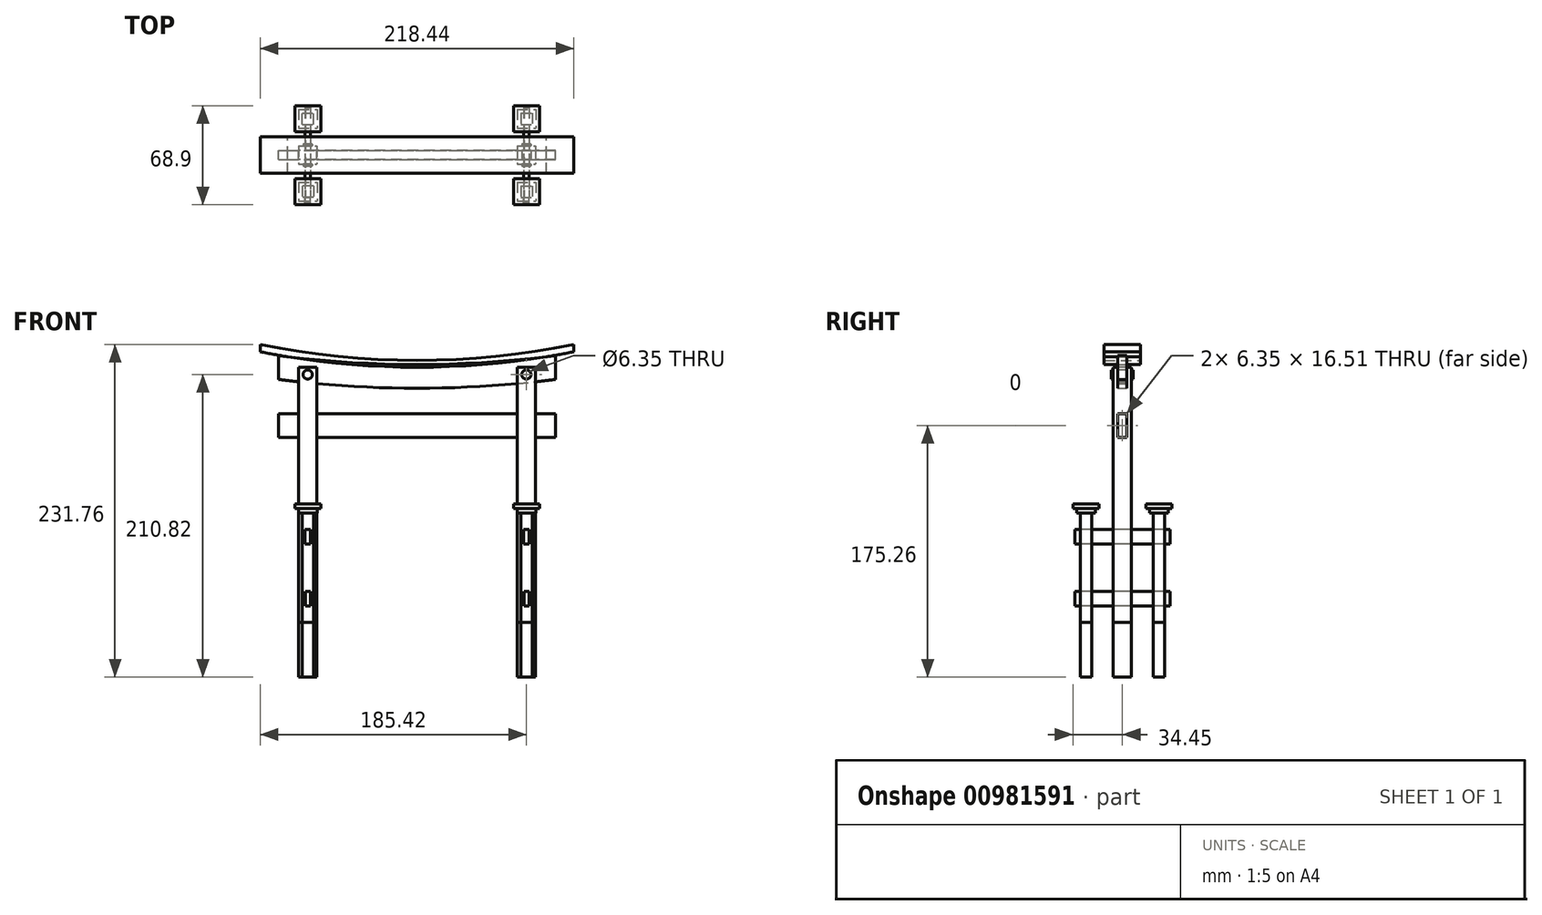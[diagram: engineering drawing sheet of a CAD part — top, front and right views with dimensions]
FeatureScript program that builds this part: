
annotation { "Feature Type Name" : "Feature", "Feature Type Description" : "" }
export const myFeature = defineFeature(function(context is Context, id is Id, definition is map)
    precondition{}
    {
        {
            var Q0;
            Q0=qCreatedBy(makeId("Top.planeOp"),FACE);
            var sketch = newSketch(context, id + "F0", { "sketchPlane" : qUnion([Q0])});
            skLineSegment(sketch, "E0.bottom", {"start": v(-82.55, 6.35) * mm, "end": v(-69.85, 6.35) * mm});
            skLineSegment(sketch, "E0.top", {"start": v(-82.55, -6.35) * mm, "end": v(-69.85, -6.35) * mm});
            skLineSegment(sketch, "E0.left", {"start": v(-82.55, 6.35) * mm, "end": v(-82.55, -6.35) * mm});
            skLineSegment(sketch, "E0.right", {"start": v(-69.85, 6.35) * mm, "end": v(-69.85, -6.35) * mm});
            skPoint(sketch, "E0.middle", {"position": v(-76.2, 0) * mm});
            skLineSegment(sketch, "E1.bottom", {"start": v(69.85, 6.35) * mm, "end": v(82.55, 6.35) * mm});
            skLineSegment(sketch, "E1.top", {"start": v(69.85, -6.35) * mm, "end": v(82.55, -6.35) * mm});
            skLineSegment(sketch, "E1.left", {"start": v(69.85, 6.35) * mm, "end": v(69.85, -6.35) * mm});
            skLineSegment(sketch, "E1.right", {"start": v(82.55, 6.35) * mm, "end": v(82.55, -6.35) * mm});
            skPoint(sketch, "E1.middle", {"position": v(76.2, 0) * mm});
            skLineSegment(sketch, "E2", {"start": v(-69.85, 0) * mm, "end": v(0, 0) * mm, "construction": true});
            skLineSegment(sketch, "E3", {"start": v(0, 0) * mm, "end": v(69.85, 0) * mm, "construction": true});
            skLineSegment(sketch, "E4.bottom", {"start": v(-80.17, 21.43) * mm, "end": v(-72.23, 21.43) * mm});
            skLineSegment(sketch, "E4.top", {"start": v(-80.17, 29.37) * mm, "end": v(-72.23, 29.37) * mm});
            skLineSegment(sketch, "E4.left", {"start": v(-80.17, 21.43) * mm, "end": v(-80.17, 29.37) * mm});
            skLineSegment(sketch, "E4.right", {"start": v(-72.23, 21.43) * mm, "end": v(-72.23, 29.37) * mm});
            skPoint(sketch, "E4.middle", {"position": v(-76.2, 25.4) * mm});
            skLineSegment(sketch, "E5.bottom", {"start": v(72.23, 29.37) * mm, "end": v(80.17, 29.37) * mm});
            skLineSegment(sketch, "E5.top", {"start": v(72.23, 21.43) * mm, "end": v(80.17, 21.43) * mm});
            skLineSegment(sketch, "E5.left", {"start": v(72.23, 29.37) * mm, "end": v(72.23, 21.43) * mm});
            skLineSegment(sketch, "E5.right", {"start": v(80.17, 29.37) * mm, "end": v(80.17, 21.43) * mm});
            skPoint(sketch, "E5.middle", {"position": v(76.2, 25.4) * mm});
            skLineSegment(sketch, "E6.bottom", {"start": v(72.23, -21.43) * mm, "end": v(80.17, -21.43) * mm});
            skLineSegment(sketch, "E6.top", {"start": v(72.23, -29.37) * mm, "end": v(80.17, -29.37) * mm});
            skLineSegment(sketch, "E6.left", {"start": v(72.23, -21.43) * mm, "end": v(72.23, -29.37) * mm});
            skLineSegment(sketch, "E6.right", {"start": v(80.17, -21.43) * mm, "end": v(80.17, -29.37) * mm});
            skPoint(sketch, "E6.middle", {"position": v(76.2, -25.4) * mm});
            skLineSegment(sketch, "E7.bottom", {"start": v(-72.23, -21.43) * mm, "end": v(-80.17, -21.43) * mm});
            skLineSegment(sketch, "E7.top", {"start": v(-72.23, -29.37) * mm, "end": v(-80.17, -29.37) * mm});
            skLineSegment(sketch, "E7.left", {"start": v(-72.23, -21.43) * mm, "end": v(-72.23, -29.37) * mm});
            skLineSegment(sketch, "E7.right", {"start": v(-80.17, -21.43) * mm, "end": v(-80.17, -29.37) * mm});
            skPoint(sketch, "E7.middle", {"position": v(-76.2, -25.4) * mm});
            skLineSegment(sketch, "E8", {"start": v(-76.2, 0) * mm, "end": v(-76.2, 25.4) * mm, "construction": true});
            skLineSegment(sketch, "E9", {"start": v(-76.2, 0) * mm, "end": v(-76.2, -25.4) * mm, "construction": true});
            skLineSegment(sketch, "E10", {"start": v(76.2, 0) * mm, "end": v(76.2, -25.4) * mm, "construction": true});
            skLineSegment(sketch, "E11", {"start": v(76.2, 25.4) * mm, "end": v(76.2, 0) * mm, "construction": true});
            skSolve(sketch);
        }
        {
            var Q0;
            Q0=makeQuery(id+"F0.imprint","IMPRINT",FACE,{"disambiguationData":[TD([[makeQuery(id+"F0.imprint","IMPRINT",EDGE,{"derivedFrom":sQuery(id+"F0.wireOp",EDGE,"E0.bottom")}),-1.0]])]});
            var Q1;
            Q1=makeQuery(id+"F0.imprint","IMPRINT",FACE,{"disambiguationData":[TD([[makeQuery(id+"F0.imprint","IMPRINT",EDGE,{"derivedFrom":sQuery(id+"F0.wireOp",EDGE,"E1.bottom")}),-1.0]])]});
            extrude(context, id + "F1", {"entities" : qUnion([Q0, Q1]), "depth" : 177.8 * mm, "offsetDistance" : 25.4 * mm});
        }
        {
            var Q0;
            Q0=makeQuery(id+"F0.imprint","IMPRINT",FACE,{"disambiguationData":[TD([[makeQuery(id+"F0.imprint","IMPRINT",EDGE,{"derivedFrom":sQuery(id+"F0.wireOp",EDGE,"E7.bottom")}),1.0]])]});
            var Q1;
            Q1=makeQuery(id+"F0.imprint","IMPRINT",FACE,{"disambiguationData":[TD([[makeQuery(id+"F0.imprint","IMPRINT",EDGE,{"derivedFrom":sQuery(id+"F0.wireOp",EDGE,"E4.bottom")}),1.0]])]});
            var Q2;
            Q2=makeQuery(id+"F0.imprint","IMPRINT",FACE,{"disambiguationData":[TD([[makeQuery(id+"F0.imprint","IMPRINT",EDGE,{"derivedFrom":sQuery(id+"F0.wireOp",EDGE,"E6.bottom")}),-1.0]])]});
            var Q3;
            Q3=makeQuery(id+"F0.imprint","IMPRINT",FACE,{"disambiguationData":[TD([[makeQuery(id+"F0.imprint","IMPRINT",EDGE,{"derivedFrom":sQuery(id+"F0.wireOp",EDGE,"E5.bottom")}),-1.0]])]});
            extrude(context, id + "F2", {"entities" : qUnion([Q0, Q1, Q2, Q3]), "depth" : 76.2 * mm, "offsetDistance" : 25.4 * mm});
        }
        {
            var Q0;
            Q0=makeQuery(id+"F2.opExtrude","CAP_FACE",FACE,{"disambiguationData":[OSD([sQuery(id+"F0.wireOp",EDGE,"E4.bottom"),sQuery(id+"F0.wireOp",EDGE,"E4.top"),sQuery(id+"F0.wireOp",EDGE,"E4.left"),sQuery(id+"F0.wireOp",EDGE,"E4.right")])],"isStart":false});
            var sketch = newSketch(context, id + "F3", { "sketchPlane" : qUnion([Q0])});
            skLineSegment(sketch, "E12.0.0", {"start": v(-72.23, 29.37) * mm, "end": v(-80.17, 29.37) * mm});
            skLineSegment(sketch, "E12.0.1", {"start": v(-80.17, 29.37) * mm, "end": v(-80.17, 21.43) * mm});
            skLineSegment(sketch, "E12.0.2", {"start": v(-80.17, 21.43) * mm, "end": v(-72.23, 21.43) * mm});
            skLineSegment(sketch, "E12.0.3", {"start": v(-72.23, 21.43) * mm, "end": v(-72.23, 29.37) * mm});
            skLineSegment(sketch, "E13.0.0", {"start": v(-80.17, -29.37) * mm, "end": v(-72.23, -29.37) * mm});
            skLineSegment(sketch, "E13.0.1", {"start": v(-72.23, -29.37) * mm, "end": v(-72.23, -21.43) * mm});
            skLineSegment(sketch, "E13.0.2", {"start": v(-72.23, -21.43) * mm, "end": v(-80.17, -21.43) * mm});
            skLineSegment(sketch, "E13.0.3", {"start": v(-80.17, -21.43) * mm, "end": v(-80.17, -29.37) * mm});
            skLineSegment(sketch, "E14.0.0", {"start": v(72.23, -21.43) * mm, "end": v(72.23, -29.37) * mm});
            skLineSegment(sketch, "E14.0.1", {"start": v(72.23, -29.37) * mm, "end": v(80.17, -29.37) * mm});
            skLineSegment(sketch, "E14.0.2", {"start": v(80.17, -29.37) * mm, "end": v(80.17, -21.43) * mm});
            skLineSegment(sketch, "E14.0.3", {"start": v(80.17, -21.43) * mm, "end": v(72.23, -21.43) * mm});
            skLineSegment(sketch, "E15.0.0", {"start": v(72.23, 29.37) * mm, "end": v(72.23, 21.43) * mm});
            skLineSegment(sketch, "E15.0.1", {"start": v(72.23, 21.43) * mm, "end": v(80.17, 21.43) * mm});
            skLineSegment(sketch, "E15.0.2", {"start": v(80.17, 21.43) * mm, "end": v(80.17, 29.37) * mm});
            skLineSegment(sketch, "E15.0.3", {"start": v(80.17, 29.37) * mm, "end": v(72.23, 29.37) * mm});
            skPoint(sketch, "E16.0", {"position": v(-76.2, 25.4) * mm});
            skPoint(sketch, "E17.0", {"position": v(-76.2, -25.4) * mm});
            skPoint(sketch, "E18.0", {"position": v(76.2, -25.4) * mm});
            skPoint(sketch, "E19.0", {"position": v(76.2, 25.4) * mm});
            skLineSegment(sketch, "E20.bottom", {"start": v(-82.7, 31.9) * mm, "end": v(-69.7, 31.9) * mm});
            skLineSegment(sketch, "E20.top", {"start": v(-82.7, 18.9) * mm, "end": v(-69.7, 18.9) * mm});
            skLineSegment(sketch, "E20.left", {"start": v(-82.7, 31.9) * mm, "end": v(-82.7, 18.9) * mm});
            skLineSegment(sketch, "E20.right", {"start": v(-69.7, 31.9) * mm, "end": v(-69.7, 18.9) * mm});
            skLineSegment(sketch, "E21.bottom", {"start": v(-82.7, -18.9) * mm, "end": v(-69.7, -18.9) * mm});
            skLineSegment(sketch, "E21.top", {"start": v(-82.7, -31.9) * mm, "end": v(-69.7, -31.9) * mm});
            skLineSegment(sketch, "E21.left", {"start": v(-82.7, -18.9) * mm, "end": v(-82.7, -31.9) * mm});
            skLineSegment(sketch, "E21.right", {"start": v(-69.7, -18.9) * mm, "end": v(-69.7, -31.9) * mm});
            skLineSegment(sketch, "E22.bottom", {"start": v(69.7, 31.9) * mm, "end": v(82.7, 31.9) * mm});
            skLineSegment(sketch, "E22.top", {"start": v(69.7, 18.9) * mm, "end": v(82.7, 18.9) * mm});
            skLineSegment(sketch, "E22.left", {"start": v(69.7, 31.9) * mm, "end": v(69.7, 18.9) * mm});
            skLineSegment(sketch, "E22.right", {"start": v(82.7, 31.9) * mm, "end": v(82.7, 18.9) * mm});
            skLineSegment(sketch, "E23.bottom", {"start": v(69.7, -18.9) * mm, "end": v(82.7, -18.9) * mm});
            skLineSegment(sketch, "E23.top", {"start": v(69.7, -31.9) * mm, "end": v(82.7, -31.9) * mm});
            skLineSegment(sketch, "E23.left", {"start": v(69.7, -18.9) * mm, "end": v(69.7, -31.9) * mm});
            skLineSegment(sketch, "E23.right", {"start": v(82.7, -18.9) * mm, "end": v(82.7, -31.9) * mm});
            skSolve(sketch);
        }
        {
            var Q0;
            Q0=makeQuery(id+"F3.imprint","IMPRINT",FACE,{"disambiguationData":[TD([[makeQuery(id+"F3.imprint","IMPRINT",EDGE,{"derivedFrom":sQuery(id+"F3.wireOp",EDGE,"E12.0.0")}),1.0]])]});
            var Q1;
            Q1=makeQuery(id+"F3.imprint","IMPRINT",FACE,{"disambiguationData":[TD([[makeQuery(id+"F3.imprint","IMPRINT",EDGE,{"derivedFrom":sQuery(id+"F3.wireOp",EDGE,"E12.0.0")}),-1.0]])]});
            var Q2;
            Q2=makeQuery(id+"F3.imprint","IMPRINT",FACE,{"disambiguationData":[TD([[makeQuery(id+"F3.imprint","IMPRINT",EDGE,{"derivedFrom":sQuery(id+"F3.wireOp",EDGE,"E15.0.0")}),1.0]])]});
            var Q3;
            Q3=makeQuery(id+"F3.imprint","IMPRINT",FACE,{"disambiguationData":[TD([[makeQuery(id+"F3.imprint","IMPRINT",EDGE,{"derivedFrom":sQuery(id+"F3.wireOp",EDGE,"E15.0.0")}),-1.0]])]});
            var Q4;
            Q4=makeQuery(id+"F3.imprint","IMPRINT",FACE,{"disambiguationData":[TD([[makeQuery(id+"F3.imprint","IMPRINT",EDGE,{"derivedFrom":sQuery(id+"F3.wireOp",EDGE,"E14.0.0")}),1.0]])]});
            var Q5;
            Q5=makeQuery(id+"F3.imprint","IMPRINT",FACE,{"disambiguationData":[TD([[makeQuery(id+"F3.imprint","IMPRINT",EDGE,{"derivedFrom":sQuery(id+"F3.wireOp",EDGE,"E14.0.0")}),-1.0]])]});
            var Q6;
            Q6=makeQuery(id+"F3.imprint","IMPRINT",FACE,{"disambiguationData":[TD([[makeQuery(id+"F3.imprint","IMPRINT",EDGE,{"derivedFrom":sQuery(id+"F3.wireOp",EDGE,"E13.0.0")}),-1.0]])]});
            var Q7;
            Q7=makeQuery(id+"F3.imprint","IMPRINT",FACE,{"disambiguationData":[TD([[makeQuery(id+"F3.imprint","IMPRINT",EDGE,{"derivedFrom":sQuery(id+"F3.wireOp",EDGE,"E13.0.0")}),1.0]])]});
            extrude(context, id + "F4", {"entities" : qUnion([Q0, Q1, Q2, Q3, Q4, Q5, Q6, Q7]), "depth" : 3.17 * mm, "offsetDistance" : 25.4 * mm});
        }
        {
            var Q0;
            Q0=makeQuery(id+"F4.opExtrude","CAP_FACE",FACE,{"disambiguationData":[OSD([sQuery(id+"F3.wireOp",EDGE,"E20.bottom"),sQuery(id+"F3.wireOp",EDGE,"E20.top"),sQuery(id+"F3.wireOp",EDGE,"E20.left"),sQuery(id+"F3.wireOp",EDGE,"E20.right")])],"isStart":false});
            var sketch = newSketch(context, id + "F5", { "sketchPlane" : qUnion([Q0])});
            skLineSegment(sketch, "E24.0.0", {"start": v(-82.7, 31.9) * mm, "end": v(-82.7, 18.9) * mm});
            skLineSegment(sketch, "E24.0.1", {"start": v(-82.7, 18.9) * mm, "end": v(-69.7, 18.9) * mm});
            skLineSegment(sketch, "E24.0.2", {"start": v(-69.7, 18.9) * mm, "end": v(-69.7, 31.9) * mm});
            skLineSegment(sketch, "E24.0.3", {"start": v(-69.7, 31.9) * mm, "end": v(-82.7, 31.9) * mm});
            skLineSegment(sketch, "E25.0.0", {"start": v(-82.7, -18.9) * mm, "end": v(-82.7, -31.9) * mm});
            skLineSegment(sketch, "E25.0.1", {"start": v(-82.7, -31.9) * mm, "end": v(-69.7, -31.9) * mm});
            skLineSegment(sketch, "E25.0.2", {"start": v(-69.7, -31.9) * mm, "end": v(-69.7, -18.9) * mm});
            skLineSegment(sketch, "E25.0.3", {"start": v(-69.7, -18.9) * mm, "end": v(-82.7, -18.9) * mm});
            skLineSegment(sketch, "E26.0.0", {"start": v(69.7, 31.9) * mm, "end": v(69.7, 18.9) * mm});
            skLineSegment(sketch, "E26.0.1", {"start": v(69.7, 18.9) * mm, "end": v(82.7, 18.9) * mm});
            skLineSegment(sketch, "E26.0.2", {"start": v(82.7, 18.9) * mm, "end": v(82.7, 31.9) * mm});
            skLineSegment(sketch, "E26.0.3", {"start": v(82.7, 31.9) * mm, "end": v(69.7, 31.9) * mm});
            skLineSegment(sketch, "E27.0.0", {"start": v(69.7, -18.9) * mm, "end": v(69.7, -31.9) * mm});
            skLineSegment(sketch, "E27.0.1", {"start": v(69.7, -31.9) * mm, "end": v(82.7, -31.9) * mm});
            skLineSegment(sketch, "E27.0.2", {"start": v(82.7, -31.9) * mm, "end": v(82.7, -18.9) * mm});
            skLineSegment(sketch, "E27.0.3", {"start": v(82.7, -18.9) * mm, "end": v(69.7, -18.9) * mm});
            skPoint(sketch, "E28.0", {"position": v(-76.2, 25.4) * mm});
            skPoint(sketch, "E29.0", {"position": v(-76.2, -25.4) * mm});
            skPoint(sketch, "E30.0", {"position": v(76.2, -25.4) * mm});
            skPoint(sketch, "E31.0", {"position": v(76.2, 25.4) * mm});
            skLineSegment(sketch, "E32.bottom", {"start": v(-85.25, 34.45) * mm, "end": v(-67.15, 34.45) * mm});
            skLineSegment(sketch, "E32.top", {"start": v(-85.25, 16.35) * mm, "end": v(-67.15, 16.35) * mm});
            skLineSegment(sketch, "E32.left", {"start": v(-85.25, 34.45) * mm, "end": v(-85.25, 16.35) * mm});
            skLineSegment(sketch, "E32.right", {"start": v(-67.15, 34.45) * mm, "end": v(-67.15, 16.35) * mm});
            skLineSegment(sketch, "E33.bottom", {"start": v(-85.25, -34.45) * mm, "end": v(-67.15, -34.45) * mm});
            skLineSegment(sketch, "E33.top", {"start": v(-85.25, -16.35) * mm, "end": v(-67.15, -16.35) * mm});
            skLineSegment(sketch, "E33.left", {"start": v(-85.25, -34.45) * mm, "end": v(-85.25, -16.35) * mm});
            skLineSegment(sketch, "E33.right", {"start": v(-67.15, -34.45) * mm, "end": v(-67.15, -16.35) * mm});
            skLineSegment(sketch, "E34.bottom", {"start": v(67.15, 16.35) * mm, "end": v(85.25, 16.35) * mm});
            skLineSegment(sketch, "E34.top", {"start": v(67.15, 34.45) * mm, "end": v(85.25, 34.45) * mm});
            skLineSegment(sketch, "E34.left", {"start": v(67.15, 16.35) * mm, "end": v(67.15, 34.45) * mm});
            skLineSegment(sketch, "E34.right", {"start": v(85.25, 16.35) * mm, "end": v(85.25, 34.45) * mm});
            skLineSegment(sketch, "E35.bottom", {"start": v(67.15, -16.35) * mm, "end": v(85.25, -16.35) * mm});
            skLineSegment(sketch, "E35.top", {"start": v(67.15, -34.45) * mm, "end": v(85.25, -34.45) * mm});
            skLineSegment(sketch, "E35.left", {"start": v(67.15, -16.35) * mm, "end": v(67.15, -34.45) * mm});
            skLineSegment(sketch, "E35.right", {"start": v(85.25, -16.35) * mm, "end": v(85.25, -34.45) * mm});
            skSolve(sketch);
        }
        {
            var Q0;
            Q0=makeQuery(id+"F5.imprint","IMPRINT",FACE,{"disambiguationData":[TD([[makeQuery(id+"F5.imprint","IMPRINT",EDGE,{"derivedFrom":sQuery(id+"F5.wireOp",EDGE,"E25.0.0")}),1.0]])]});
            var Q1;
            Q1=makeQuery(id+"F5.imprint","IMPRINT",FACE,{"disambiguationData":[TD([[makeQuery(id+"F5.imprint","IMPRINT",EDGE,{"derivedFrom":sQuery(id+"F5.wireOp",EDGE,"E25.0.0")}),-1.0]])]});
            var Q2;
            Q2=makeQuery(id+"F5.imprint","IMPRINT",FACE,{"disambiguationData":[TD([[makeQuery(id+"F5.imprint","IMPRINT",EDGE,{"derivedFrom":sQuery(id+"F5.wireOp",EDGE,"E27.0.0")}),-1.0]])]});
            var Q3;
            Q3=makeQuery(id+"F5.imprint","IMPRINT",FACE,{"disambiguationData":[TD([[makeQuery(id+"F5.imprint","IMPRINT",EDGE,{"derivedFrom":sQuery(id+"F5.wireOp",EDGE,"E27.0.0")}),1.0]])]});
            var Q4;
            Q4=makeQuery(id+"F5.imprint","IMPRINT",FACE,{"disambiguationData":[TD([[makeQuery(id+"F5.imprint","IMPRINT",EDGE,{"derivedFrom":sQuery(id+"F5.wireOp",EDGE,"E26.0.0")}),1.0]])]});
            var Q5;
            Q5=makeQuery(id+"F5.imprint","IMPRINT",FACE,{"disambiguationData":[TD([[makeQuery(id+"F5.imprint","IMPRINT",EDGE,{"derivedFrom":sQuery(id+"F5.wireOp",EDGE,"E26.0.0")}),-1.0]])]});
            var Q6;
            Q6=makeQuery(id+"F5.imprint","IMPRINT",FACE,{"disambiguationData":[TD([[makeQuery(id+"F5.imprint","IMPRINT",EDGE,{"derivedFrom":sQuery(id+"F5.wireOp",EDGE,"E24.0.0")}),1.0]])]});
            var Q7;
            Q7=makeQuery(id+"F5.imprint","IMPRINT",FACE,{"disambiguationData":[TD([[makeQuery(id+"F5.imprint","IMPRINT",EDGE,{"derivedFrom":sQuery(id+"F5.wireOp",EDGE,"E24.0.0")}),-1.0]])]});
            extrude(context, id + "F6", {"entities" : qUnion([Q0, Q1, Q2, Q3, Q4, Q5, Q6, Q7]), "depth" : 3.17 * mm, "offsetDistance" : 25.4 * mm});
        }
        {
            var Q0;
            Q0=makeQuery(id+"F2.opExtrude","SWEPT_FACE",FACE,{"disambiguationData":[OSD([sQuery(id+"F0.wireOp",EDGE,"E7.top")])]});
            var sketch = newSketch(context, id + "F7", { "sketchPlane" : qUnion([Q0])});
            skLineSegment(sketch, "E36.0.0", {"start": v(-80.17, 0) * mm, "end": v(-72.23, 0) * mm});
            skLineSegment(sketch, "E36.0.1", {"start": v(-72.23, 0) * mm, "end": v(-72.23, 76.2) * mm});
            skLineSegment(sketch, "E36.0.2", {"start": v(-72.23, 76.2) * mm, "end": v(-80.17, 76.2) * mm});
            skLineSegment(sketch, "E36.0.3", {"start": v(-80.17, 76.2) * mm, "end": v(-80.17, 0) * mm});
            skLineSegment(sketch, "E37.0.0", {"start": v(72.23, 0) * mm, "end": v(80.17, 0) * mm});
            skLineSegment(sketch, "E37.0.1", {"start": v(80.17, 0) * mm, "end": v(80.17, 76.2) * mm});
            skLineSegment(sketch, "E37.0.2", {"start": v(80.17, 76.2) * mm, "end": v(72.23, 76.2) * mm});
            skLineSegment(sketch, "E37.0.3", {"start": v(72.23, 76.2) * mm, "end": v(72.23, 0) * mm});
            skLineSegment(sketch, "E38", {"start": v(-76.2, 76.2) * mm, "end": v(-76.2, 0) * mm, "construction": true});
            skLineSegment(sketch, "E39", {"start": v(76.2, 76.2) * mm, "end": v(76.2, 0) * mm, "construction": true});
            skLineSegment(sketch, "E40.bottom", {"start": v(-77.97, 64.77) * mm, "end": v(-74.43, 64.77) * mm});
            skLineSegment(sketch, "E40.top", {"start": v(-77.97, 54.6) * mm, "end": v(-74.43, 54.6) * mm});
            skLineSegment(sketch, "E40.left", {"start": v(-77.97, 64.77) * mm, "end": v(-77.97, 54.6) * mm});
            skLineSegment(sketch, "E40.right", {"start": v(-74.43, 64.77) * mm, "end": v(-74.43, 54.61) * mm});
            skPoint(sketch, "E40.middle", {"position": v(-76.2, 59.69) * mm});
            skLineSegment(sketch, "E41.bottom", {"start": v(-77.94, 21.6) * mm, "end": v(-74.46, 21.6) * mm});
            skLineSegment(sketch, "E41.top", {"start": v(-77.94, 11.43) * mm, "end": v(-74.46, 11.43) * mm});
            skLineSegment(sketch, "E41.left", {"start": v(-77.94, 21.6) * mm, "end": v(-77.94, 11.43) * mm});
            skLineSegment(sketch, "E41.right", {"start": v(-74.46, 21.6) * mm, "end": v(-74.46, 11.43) * mm});
            skPoint(sketch, "E41.middle", {"position": v(-76.2, 16.51) * mm});
            skLineSegment(sketch, "E42.bottom", {"start": v(74.43, 64.77) * mm, "end": v(77.97, 64.77) * mm});
            skLineSegment(sketch, "E42.top", {"start": v(74.43, 54.6) * mm, "end": v(77.97, 54.6) * mm});
            skLineSegment(sketch, "E42.left", {"start": v(74.43, 64.77) * mm, "end": v(74.43, 54.6) * mm});
            skLineSegment(sketch, "E42.right", {"start": v(77.97, 64.77) * mm, "end": v(77.97, 54.6) * mm});
            skPoint(sketch, "E42.middle", {"position": v(76.2, 59.69) * mm});
            skLineSegment(sketch, "E43.bottom", {"start": v(74.46, 21.6) * mm, "end": v(77.94, 21.6) * mm});
            skLineSegment(sketch, "E43.top", {"start": v(74.46, 11.43) * mm, "end": v(77.94, 11.43) * mm});
            skLineSegment(sketch, "E43.left", {"start": v(74.46, 21.6) * mm, "end": v(74.46, 11.43) * mm});
            skLineSegment(sketch, "E43.right", {"start": v(77.94, 21.6) * mm, "end": v(77.94, 11.43) * mm});
            skPoint(sketch, "E43.middle", {"position": v(76.2, 16.51) * mm});
            skLineSegment(sketch, "E44", {"start": v(-76.2, 76.2) * mm, "end": v(-77.97, 64.77) * mm, "construction": true});
            skLineSegment(sketch, "E45", {"start": v(-77.97, 54.6) * mm, "end": v(-77.94, 21.6) * mm, "construction": true});
            skLineSegment(sketch, "E46", {"start": v(-77.94, 11.43) * mm, "end": v(-76.2, 0) * mm, "construction": true});
            skLineSegment(sketch, "E47", {"start": v(76.2, 0) * mm, "end": v(77.94, 11.43) * mm, "construction": true});
            skLineSegment(sketch, "E48", {"start": v(77.94, 21.6) * mm, "end": v(77.97, 54.6) * mm, "construction": true});
            skLineSegment(sketch, "E49", {"start": v(77.97, 64.77) * mm, "end": v(76.2, 76.2) * mm, "construction": true});
            skSolve(sketch);
        }
        {
            var Q0;
            Q0=makeQuery(id+"F7.imprint","IMPRINT",FACE,{"disambiguationData":[TD([[makeQuery(id+"F7.imprint","IMPRINT",EDGE,{"derivedFrom":sQuery(id+"F7.wireOp",EDGE,"E40.bottom")}),-1.0]])]});
            var Q1;
            Q1=makeQuery(id+"F7.imprint","IMPRINT",FACE,{"disambiguationData":[TD([[makeQuery(id+"F7.imprint","IMPRINT",EDGE,{"derivedFrom":sQuery(id+"F7.wireOp",EDGE,"E41.bottom")}),-1.0]])]});
            var Q2;
            Q2=makeQuery(id+"F7.imprint","IMPRINT",FACE,{"disambiguationData":[TD([[makeQuery(id+"F7.imprint","IMPRINT",EDGE,{"derivedFrom":sQuery(id+"F7.wireOp",EDGE,"E42.bottom")}),-1.0]])]});
            var Q3;
            Q3=makeQuery(id+"F7.imprint","IMPRINT",FACE,{"disambiguationData":[TD([[makeQuery(id+"F7.imprint","IMPRINT",EDGE,{"derivedFrom":sQuery(id+"F7.wireOp",EDGE,"E43.bottom")}),-1.0]])]});
            extrude(context, id + "F8", {"entities" : qUnion([Q0, Q1, Q2, Q3]), "depth" : 3.8 * mm, "offsetDistance" : 25.4 * mm});
        }
        {
            var Q0;
            Q0=makeQuery(id+"F7.imprint","IMPRINT",FACE,{"disambiguationData":[TD([[makeQuery(id+"F7.imprint","IMPRINT",EDGE,{"derivedFrom":sQuery(id+"F7.wireOp",EDGE,"E40.bottom")}),-1.0]])]});
            var Q1;
            Q1=makeQuery(id+"F7.imprint","IMPRINT",FACE,{"disambiguationData":[TD([[makeQuery(id+"F7.imprint","IMPRINT",EDGE,{"derivedFrom":sQuery(id+"F7.wireOp",EDGE,"E41.bottom")}),-1.0]])]});
            var Q2;
            Q2=makeQuery(id+"F7.imprint","IMPRINT",FACE,{"disambiguationData":[TD([[makeQuery(id+"F7.imprint","IMPRINT",EDGE,{"derivedFrom":sQuery(id+"F7.wireOp",EDGE,"E42.bottom")}),-1.0]])]});
            var Q3;
            Q3=makeQuery(id+"F7.imprint","IMPRINT",FACE,{"disambiguationData":[TD([[makeQuery(id+"F7.imprint","IMPRINT",EDGE,{"derivedFrom":sQuery(id+"F7.wireOp",EDGE,"E43.bottom")}),-1.0]])]});
            extrude(context, id + "F9", {"entities" : qUnion([Q0, Q1, Q2, Q3]), "oppositeDirection" : true, "depth" : 62.55 * mm, "offsetDistance" : 25.4 * mm});
        }
        {
            var Q0;
            Q0=makeQuery(id+"F1.opExtrude","SWEPT_FACE",FACE,{"disambiguationData":[OSD([sQuery(id+"F0.wireOp",EDGE,"E0.right")])]});
            var sketch = newSketch(context, id + "F10", { "sketchPlane" : qUnion([Q0])});
            skLineSegment(sketch, "E50.0.0", {"start": v(-6.35, 0) * mm, "end": v(6.35, 0) * mm});
            skLineSegment(sketch, "E50.0.1", {"start": v(6.35, 0) * mm, "end": v(6.35, 177.8) * mm});
            skLineSegment(sketch, "E50.0.2", {"start": v(6.35, 177.8) * mm, "end": v(-6.35, 177.8) * mm});
            skLineSegment(sketch, "E50.0.3", {"start": v(-6.35, 177.8) * mm, "end": v(-6.35, 0) * mm});
            skLineSegment(sketch, "E51", {"start": v(0, 177.8) * mm, "end": v(0, 0) * mm, "construction": true});
            skLineSegment(sketch, "E52", {"start": v(0, 177.8) * mm, "end": v(0, 137.16) * mm, "construction": true});
            skLineSegment(sketch, "E53.bottom", {"start": v(-3.18, 145.42) * mm, "end": v(3.17, 145.42) * mm});
            skLineSegment(sketch, "E53.top", {"start": v(-3.18, 128.9) * mm, "end": v(3.17, 128.9) * mm});
            skLineSegment(sketch, "E53.left", {"start": v(-3.18, 145.42) * mm, "end": v(-3.18, 128.9) * mm});
            skLineSegment(sketch, "E53.right", {"start": v(3.17, 145.42) * mm, "end": v(3.17, 128.9) * mm});
            skPoint(sketch, "E53.middle", {"position": v(0, 137.16) * mm});
            skLineSegment(sketch, "E54", {"start": v(0, 137.16) * mm, "end": v(0, 177.8) * mm, "construction": true});
            skLineSegment(sketch, "E55.bottom", {"start": v(-3.18, 169.55) * mm, "end": v(3.17, 169.55) * mm});
            skLineSegment(sketch, "E55.top", {"start": v(-3.18, 186.06) * mm, "end": v(3.17, 186.06) * mm});
            skLineSegment(sketch, "E55.left", {"start": v(-3.18, 169.55) * mm, "end": v(-3.18, 186.06) * mm});
            skLineSegment(sketch, "E55.right", {"start": v(3.17, 169.55) * mm, "end": v(3.17, 186.06) * mm});
            skPoint(sketch, "E55.middle", {"position": v(0, 177.8) * mm});
            skLineSegment(sketch, "E56.bottom", {"start": v(-9.01, 189.87) * mm, "end": v(9.01, 189.87) * mm});
            skLineSegment(sketch, "E56.top", {"start": v(-9.01, 182.25) * mm, "end": v(9.01, 182.25) * mm});
            skLineSegment(sketch, "E56.left", {"start": v(-9.01, 189.87) * mm, "end": v(-9.01, 182.25) * mm});
            skLineSegment(sketch, "E56.right", {"start": v(9.01, 189.87) * mm, "end": v(9.01, 182.25) * mm});
            skPoint(sketch, "E56.middle", {"position": v(0, 186.06) * mm});
            skSolve(sketch);
        }
        {
            var Q0;
            Q0=makeQuery(id+"F10.imprint","IMPRINT",FACE,{"disambiguationData":[TD([[makeQuery(id+"F10.imprint","IMPRINT",EDGE,{"derivedFrom":sQuery(id+"F10.wireOp",EDGE,"E53.bottom")}),-1.0]])]});
            extrude(context, id + "F11", {"entities" : qUnion([Q0]), "operationType" : NewBodyOperationType.ADD, "oppositeDirection" : true, "depth" : 26.67 * mm, "offsetDistance" : 25.4 * mm});
        }
        {
            var Q0;
            Q0=makeQuery(id+"F10.imprint","IMPRINT",FACE,{"disambiguationData":[TD([[makeQuery(id+"F10.imprint","IMPRINT",EDGE,{"derivedFrom":sQuery(id+"F10.wireOp",EDGE,"E53.bottom")}),-1.0]])]});
            extrude(context, id + "F12", {"entities" : qUnion([Q0]), "operationType" : NewBodyOperationType.ADD, "depth" : 166.37 * mm, "offsetDistance" : 25.4 * mm});
        }
        {
            var Q0;
            Q0=qCreatedBy(makeId("Front.planeOp"),FACE);
            var sketch = newSketch(context, id + "F13", { "sketchPlane" : qUnion([Q0])});
            skLineSegment(sketch, "E57.0.0", {"start": v(-69.85, 145.42) * mm, "end": v(-69.85, 128.9) * mm});
            skLineSegment(sketch, "E57.0.1", {"start": v(-69.85, 128.9) * mm, "end": v(96.52, 128.9) * mm});
            skLineSegment(sketch, "E57.0.2", {"start": v(96.52, 128.9) * mm, "end": v(96.52, 145.42) * mm});
            skLineSegment(sketch, "E57.0.3", {"start": v(96.52, 145.42) * mm, "end": v(-69.85, 145.42) * mm});
            skLineSegment(sketch, "E58.0.0", {"start": v(-82.55, 128.9) * mm, "end": v(-82.55, 145.42) * mm});
            skLineSegment(sketch, "E58.0.1", {"start": v(-82.55, 145.42) * mm, "end": v(-96.52, 145.42) * mm});
            skLineSegment(sketch, "E58.0.2", {"start": v(-96.52, 145.42) * mm, "end": v(-96.52, 128.9) * mm});
            skLineSegment(sketch, "E58.0.3", {"start": v(-96.52, 128.9) * mm, "end": v(-82.55, 128.9) * mm});
            skLineSegment(sketch, "E59.0.0", {"start": v(69.85, 0) * mm, "end": v(82.55, 0) * mm});
            skLineSegment(sketch, "E59.0.1", {"start": v(82.55, 0) * mm, "end": v(82.55, 177.8) * mm});
            skLineSegment(sketch, "E59.0.2", {"start": v(82.55, 177.8) * mm, "end": v(69.85, 177.8) * mm});
            skLineSegment(sketch, "E59.0.3", {"start": v(69.85, 177.8) * mm, "end": v(69.85, 0) * mm});
            skLineSegment(sketch, "E60.0.0", {"start": v(-82.55, 0) * mm, "end": v(-69.85, 0) * mm});
            skLineSegment(sketch, "E60.0.1", {"start": v(-69.85, 0) * mm, "end": v(-69.85, 177.8) * mm});
            skLineSegment(sketch, "E60.0.2", {"start": v(-69.85, 177.8) * mm, "end": v(-82.55, 177.8) * mm});
            skLineSegment(sketch, "E60.0.3", {"start": v(-82.55, 177.8) * mm, "end": v(-82.55, 0) * mm});
            skLineSegment(sketch, "E61", {"start": v(0, 0) * mm, "end": v(0, 137.16) * mm, "construction": true});
            skPoint(sketch, "E61.endSnap0", {"position": v(-96.52, 137.16) * mm});
            skLineSegment(sketch, "E62", {"start": v(0, 137.16) * mm, "end": v(0, 169.54) * mm, "construction": true});
            skLineSegment(sketch, "E63.0.0", {"start": v(-96.52, 163.2) * mm, "end": v(-82.55, 163.2) * mm});
            skLineSegment(sketch, "E63.0.1", {"start": v(-82.55, 163.2) * mm, "end": v(-82.55, 177.8) * mm});
            skLineSegment(sketch, "E63.0.2", {"start": v(-82.55, 177.8) * mm, "end": v(-69.85, 177.8) * mm});
            skLineSegment(sketch, "E63.0.3", {"start": v(-69.85, 177.8) * mm, "end": v(-69.85, 163.2) * mm});
            skLineSegment(sketch, "E63.0.4", {"start": v(-69.85, 163.2) * mm, "end": v(96.52, 163.2) * mm});
            skLineSegment(sketch, "E63.0.5", {"start": v(96.52, 163.2) * mm, "end": v(96.52, 192.4) * mm});
            skLineSegment(sketch, "E63.0.6", {"start": v(96.52, 192.4) * mm, "end": v(-96.52, 192.4) * mm});
            skLineSegment(sketch, "E63.0.7", {"start": v(-96.52, 192.4) * mm, "end": v(-96.52, 163.2) * mm});
            skLineSegment(sketch, "E64", {"start": v(-82.55, 163.2) * mm, "end": v(-69.85, 163.2) * mm});
            skLineSegment(sketch, "E65", {"start": v(0, 162.29) * mm, "end": v(0, 163.2) * mm, "construction": true});
            skLineSegment(sketch, "E66", {"start": v(0, 163.2) * mm, "end": v(0, 179.7) * mm, "construction": true});
            skArc(sketch, "E67", {"start": v(-96.52, 185.93) * mm, "mid": v(0, 179.7) * mm, "end": v(96.52, 185.93) * mm});
            skArc(sketch, "E68", {"start": v(-96.52, 169.28) * mm, "mid": v(0, 163.2) * mm, "end": v(96.52, 169.28) * mm});
            skLineSegment(sketch, "E69", {"start": v(-96.52, 177.8) * mm, "end": v(0, 177.8) * mm, "construction": true});
            skLineSegment(sketch, "E70", {"start": v(0, 177.8) * mm, "end": v(96.52, 177.8) * mm, "construction": true});
            skLineSegment(sketch, "E71", {"start": v(0, 192.4) * mm, "end": v(0, 177.8) * mm, "construction": true});
            skLineSegment(sketch, "E72.bottom", {"start": v(-109.22, 201.28) * mm, "end": v(109.22, 201.28) * mm});
            skLineSegment(sketch, "E72.top", {"start": v(-109.22, 158.13) * mm, "end": v(109.22, 158.13) * mm});
            skLineSegment(sketch, "E72.left", {"start": v(-109.22, 201.28) * mm, "end": v(-109.22, 158.13) * mm});
            skLineSegment(sketch, "E72.right", {"start": v(109.22, 201.28) * mm, "end": v(109.22, 158.13) * mm});
            skPoint(sketch, "E72.middle", {"position": v(0, 179.7) * mm});
            skLineSegment(sketch, "E73", {"start": v(-109.22, 201.28) * mm, "end": v(-109.22, 193.66) * mm, "construction": true});
            skLineSegment(sketch, "E74", {"start": v(109.22, 201.28) * mm, "end": v(109.22, 193.66) * mm, "construction": true});
            skLineSegment(sketch, "E75", {"start": v(-109.22, 193.66) * mm, "end": v(-109.22, 188.58) * mm, "construction": true});
            skLineSegment(sketch, "E76", {"start": v(109.22, 193.66) * mm, "end": v(109.22, 188.58) * mm, "construction": true});
            skArc(sketch, "E77", {"start": v(-109.22, 188.58) * mm, "mid": v(0, 177.8) * mm, "end": v(109.22, 188.58) * mm});
            skArc(sketch, "E78", {"start": v(-109.22, 193.66) * mm, "mid": v(0, 182.53) * mm, "end": v(109.22, 193.66) * mm});
            skSolve(sketch);
        }
        {
            var Q0;
            {var subQ5=sQuery(id+"F13.wireOp",EDGE,"E59.0.2");Q0=makeQuery(id+"F13.imprint","IMPRINT",FACE,{"disambiguationData":[TD([[makeQuery(id+"F13.imprint","IMPRINT",EDGE,{"derivedFrom":subQ5}),-1.0]])]});}
            var Q1;
            {var subQ0=sQuery(id+"F13.wireOp",EDGE,"E63.0.2");Q1=makeQuery(id+"F13.imprint","IMPRINT",FACE,{"disambiguationData":[TD([[makeQuery(id+"F13.imprint","IMPRINT",EDGE,{"derivedFrom":subQ0}),-1.0]])]});}
            var Q2;
            {var subQ0=sQuery(id+"F13.wireOp",EDGE,"E59.0.2");Q2=makeQuery(id+"F13.imprint","IMPRINT",FACE,{"disambiguationData":[TD([[makeQuery(id+"F13.imprint","IMPRINT",EDGE,{"derivedFrom":subQ0}),1.0]])]});}
            extrude(context, id + "F14", {"entities" : qUnion([Q0, Q1, Q2]), "endBound" : BoundingType.SYMMETRIC, "depth" : 6.35 * mm, "offsetDistance" : 25.4 * mm});
        }
        {
            var Q0;
            {var subQ0=sQuery(id+"F13.wireOp",EDGE,"E78");var subQ1=sQuery(id+"F13.wireOp",EDGE,"E63.0.7");var subQ2=makeQuery(id+"F13.imprint","INTERSECT",VERTEX,{"derivedFrom":[subQ1,subQ0]});Q0=makeQuery(id+"F13.imprint","IMPRINT",FACE,{"disambiguationData":[TD([[makeQuery(id+"F13.imprint","IMPRINT",EDGE,{"disambiguationData":[TD([[subQ2,-1.0]])],"derivedFrom":subQ1}),-1.0]])]});}
            var Q1;
            {var subQ0=sQuery(id+"F13.wireOp",EDGE,"E77");var subQ8=sQuery(id+"F13.wireOp",EDGE,"E63.0.5");var subQ9=makeQuery(id+"F13.imprint","INTERSECT",VERTEX,{"derivedFrom":[subQ8,subQ0]});Q1=makeQuery(id+"F13.imprint","IMPRINT",FACE,{"disambiguationData":[TD([[makeQuery(id+"F13.imprint","IMPRINT",EDGE,{"disambiguationData":[TD([[subQ9,-1.0]])],"derivedFrom":subQ8}),1.0]])]});}
            var Q2;
            {var subQ0=sQuery(id+"F13.wireOp",EDGE,"E77");var subQ1=sQuery(id+"F13.wireOp",EDGE,"E63.0.5");var subQ2=makeQuery(id+"F13.imprint","INTERSECT",VERTEX,{"derivedFrom":[subQ1,subQ0]});Q2=makeQuery(id+"F13.imprint","IMPRINT",FACE,{"disambiguationData":[TD([[makeQuery(id+"F13.imprint","IMPRINT",EDGE,{"disambiguationData":[TD([[subQ2,-1.0]])],"derivedFrom":subQ1}),-1.0]])]});}
            extrude(context, id + "F15", {"entities" : qUnion([Q0, Q1, Q2]), "endBound" : BoundingType.SYMMETRIC, "depth" : 25.4 * mm, "offsetDistance" : 25.4 * mm});
        }
        {
            var Q0;
            Q0=makeQuery(id+"F1.opExtrude","SWEPT_FACE",FACE,{"disambiguationData":[OSD([sQuery(id+"F0.wireOp",EDGE,"E0.top")])]});
            var sketch = newSketch(context, id + "F16", { "sketchPlane" : qUnion([Q0])});
            skLineSegment(sketch, "E79.0.0", {"start": v(-96.52, 185.93) * mm, "end": v(-96.52, 169.28) * mm});
            skArc(sketch, "E79.0.1", {"start": v(-96.52, 169.28) * mm, "mid": v(0, 163.2) * mm, "end": v(96.52, 169.28) * mm});
            skLineSegment(sketch, "E79.0.2", {"start": v(96.52, 169.28) * mm, "end": v(96.52, 185.93) * mm});
            skArc(sketch, "E79.0.3", {"start": v(96.52, 185.93) * mm, "mid": v(93.4, 185.53) * mm, "end": v(90.3, 185.15) * mm});
            skArc(sketch, "E79.0.4", {"start": v(90.3, 185.15) * mm, "mid": v(0, 177.8) * mm, "end": v(-90.3, 185.15) * mm});
            skArc(sketch, "E79.0.5", {"start": v(-90.3, 185.15) * mm, "mid": v(-93.4, 185.53) * mm, "end": v(-96.52, 185.93) * mm});
            skLineSegment(sketch, "E80", {"start": v(-76.2, 177.8) * mm, "end": v(-76.2, 172.72) * mm, "construction": true});
            skCircle(sketch, "E81", {"center": v(-76.2, 172.72) * mm, "radius": 3.18 * mm});
            skLineSegment(sketch, "E82.0.0", {"start": v(69.85, 0) * mm, "end": v(82.55, 0) * mm, "construction": true});
            skLineSegment(sketch, "E82.0.1", {"start": v(82.55, 0) * mm, "end": v(82.55, 177.8) * mm, "construction": true});
            skLineSegment(sketch, "E82.0.2", {"start": v(82.55, 177.8) * mm, "end": v(69.85, 177.8) * mm, "construction": true});
            skLineSegment(sketch, "E82.0.3", {"start": v(69.85, 177.8) * mm, "end": v(69.85, 0) * mm, "construction": true});
            skLineSegment(sketch, "E83", {"start": v(76.2, 177.8) * mm, "end": v(76.2, 172.72) * mm, "construction": true});
            skCircle(sketch, "E84", {"center": v(76.2, 172.72) * mm, "radius": 3.18 * mm});
            skSolve(sketch);
        }
        {
            var Q0;
            Q0=makeQuery(id+"F16.imprint","IMPRINT",FACE,{"disambiguationData":[TD([[makeQuery(id+"F16.imprint","IMPRINT",EDGE,{"derivedFrom":sQuery(id+"F16.wireOp",EDGE,"E81")}),1.0]])]});
            extrude(context, id + "F17", {"entities" : qUnion([Q0]), "operationType" : NewBodyOperationType.REMOVE, "oppositeDirection" : true, "depth" : 25.4 * mm, "offsetDistance" : 25.4 * mm});
        }
        {
            var Q0;
            Q0=makeQuery(id+"F16.imprint","IMPRINT",FACE,{"disambiguationData":[TD([[makeQuery(id+"F16.imprint","IMPRINT",EDGE,{"derivedFrom":sQuery(id+"F16.wireOp",EDGE,"E81")}),1.0]])]});
            extrude(context, id + "F18", {"entities" : qUnion([Q0]), "oppositeDirection" : true, "depth" : 13.97 * mm, "offsetDistance" : 25.4 * mm});
        }
        {
            var Q0;
            Q0=makeQuery(id+"F16.imprint","IMPRINT",FACE,{"disambiguationData":[TD([[makeQuery(id+"F16.imprint","IMPRINT",EDGE,{"derivedFrom":sQuery(id+"F16.wireOp",EDGE,"E81")}),1.0]])]});
            extrude(context, id + "F19", {"entities" : qUnion([Q0]), "operationType" : NewBodyOperationType.ADD, "depth" : 1.27 * mm, "offsetDistance" : 25.4 * mm});
        }
        {
            var Q0;
            Q0=makeQuery(id+"F16.imprint","IMPRINT",FACE,{"disambiguationData":[TD([[makeQuery(id+"F16.imprint","IMPRINT",EDGE,{"derivedFrom":sQuery(id+"F16.wireOp",EDGE,"E84")}),1.0]])]});
            extrude(context, id + "F20", {"entities" : qUnion([Q0]), "operationType" : NewBodyOperationType.REMOVE, "oppositeDirection" : true, "depth" : 25.4 * mm, "offsetDistance" : 25.4 * mm});
        }
        {
            var Q0;
            Q0=makeQuery(id+"F16.imprint","IMPRINT",FACE,{"disambiguationData":[TD([[makeQuery(id+"F16.imprint","IMPRINT",EDGE,{"derivedFrom":sQuery(id+"F16.wireOp",EDGE,"E84")}),1.0]])]});
            extrude(context, id + "F21", {"entities" : qUnion([Q0]), "oppositeDirection" : true, "depth" : 13.97 * mm, "offsetDistance" : 25.4 * mm});
        }
        {
            var Q0;
            Q0=makeQuery(id+"F16.imprint","IMPRINT",FACE,{"disambiguationData":[TD([[makeQuery(id+"F16.imprint","IMPRINT",EDGE,{"derivedFrom":sQuery(id+"F16.wireOp",EDGE,"E84")}),1.0]])]});
            extrude(context, id + "F22", {"entities" : qUnion([Q0]), "operationType" : NewBodyOperationType.ADD, "depth" : 1.27 * mm, "offsetDistance" : 25.4 * mm});
        }
        {
            var Q0;
            Q0=makeQuery(id+"F2.opExtrude","CAP_FACE",FACE,{"disambiguationData":[OSD([sQuery(id+"F0.wireOp",EDGE,"E7.bottom"),sQuery(id+"F0.wireOp",EDGE,"E7.top"),sQuery(id+"F0.wireOp",EDGE,"E7.left"),sQuery(id+"F0.wireOp",EDGE,"E7.right")])],"isStart":true});
            var Q1;
            Q1=makeQuery(id+"F1.opExtrude","CAP_FACE",FACE,{"disambiguationData":[OSD([sQuery(id+"F0.wireOp",EDGE,"E0.bottom"),sQuery(id+"F0.wireOp",EDGE,"E0.top"),sQuery(id+"F0.wireOp",EDGE,"E0.left"),sQuery(id+"F0.wireOp",EDGE,"E0.right")])],"isStart":true});
            var Q2;
            Q2=makeQuery(id+"F2.opExtrude","CAP_FACE",FACE,{"disambiguationData":[OSD([sQuery(id+"F0.wireOp",EDGE,"E4.bottom"),sQuery(id+"F0.wireOp",EDGE,"E4.top"),sQuery(id+"F0.wireOp",EDGE,"E4.left"),sQuery(id+"F0.wireOp",EDGE,"E4.right")])],"isStart":true});
            var Q3;
            Q3=makeQuery(id+"F2.opExtrude","CAP_FACE",FACE,{"disambiguationData":[OSD([sQuery(id+"F0.wireOp",EDGE,"E6.bottom"),sQuery(id+"F0.wireOp",EDGE,"E6.top"),sQuery(id+"F0.wireOp",EDGE,"E6.left"),sQuery(id+"F0.wireOp",EDGE,"E6.right")])],"isStart":true});
            var Q4;
            Q4=makeQuery(id+"F1.opExtrude","CAP_FACE",FACE,{"disambiguationData":[OSD([sQuery(id+"F0.wireOp",EDGE,"E1.bottom"),sQuery(id+"F0.wireOp",EDGE,"E1.top"),sQuery(id+"F0.wireOp",EDGE,"E1.left"),sQuery(id+"F0.wireOp",EDGE,"E1.right")])],"isStart":true});
            var Q5;
            Q5=makeQuery(id+"F2.opExtrude","CAP_FACE",FACE,{"disambiguationData":[OSD([sQuery(id+"F0.wireOp",EDGE,"E5.bottom"),sQuery(id+"F0.wireOp",EDGE,"E5.top"),sQuery(id+"F0.wireOp",EDGE,"E5.left"),sQuery(id+"F0.wireOp",EDGE,"E5.right")])],"isStart":true});
            extrude(context, id + "F23", {"entities" : qUnion([Q0, Q1, Q2, Q3, Q4, Q5]), "depth" : 38.1 * mm, "offsetDistance" : 25.4 * mm});
        }
    });
